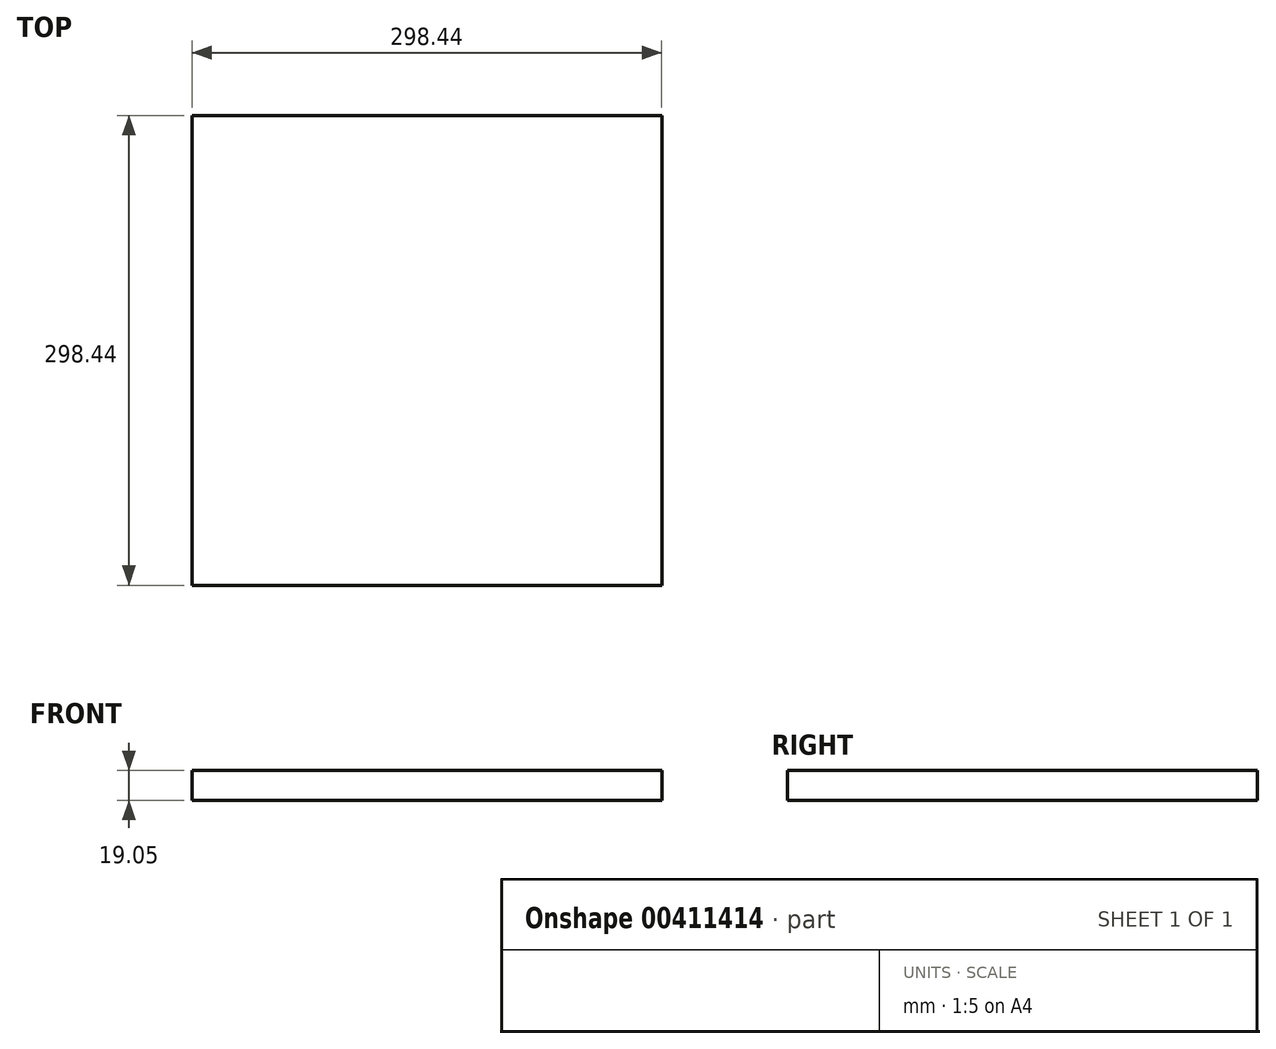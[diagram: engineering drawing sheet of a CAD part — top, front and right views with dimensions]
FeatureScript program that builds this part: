
annotation { "Feature Type Name" : "Feature", "Feature Type Description" : "" }
export const myFeature = defineFeature(function(context is Context, id is Id, definition is map)
    precondition{}
    {
        {
            var Q0;
            Q0=qCreatedBy(makeId("Top.planeOp"),FACE);
            var sketch = newSketch(context, id + "F0", { "sketchPlane" : qUnion([Q0])});
            skLineSegment(sketch, "E0.bottom", {"start": v(149.22, 149.23) * mm, "end": v(-149.23, 149.22) * mm});
            skLineSegment(sketch, "E0.top", {"start": v(149.23, -149.22) * mm, "end": v(-149.22, -149.23) * mm});
            skLineSegment(sketch, "E0.left", {"start": v(149.22, 149.23) * mm, "end": v(149.23, -149.22) * mm});
            skLineSegment(sketch, "E0.right", {"start": v(-149.23, 149.22) * mm, "end": v(-149.22, -149.23) * mm});
            skPoint(sketch, "E0.middle", {"position": v(0, 0) * mm});
            skSolve(sketch);
        }
        {
            var Q0;
            Q0 = qSketchRegion(id + "F0", true);
            extrude(context, id + "F1", {"entities" : qUnion([Q0]), "depth" : 19.05 * mm});
        }
    });
